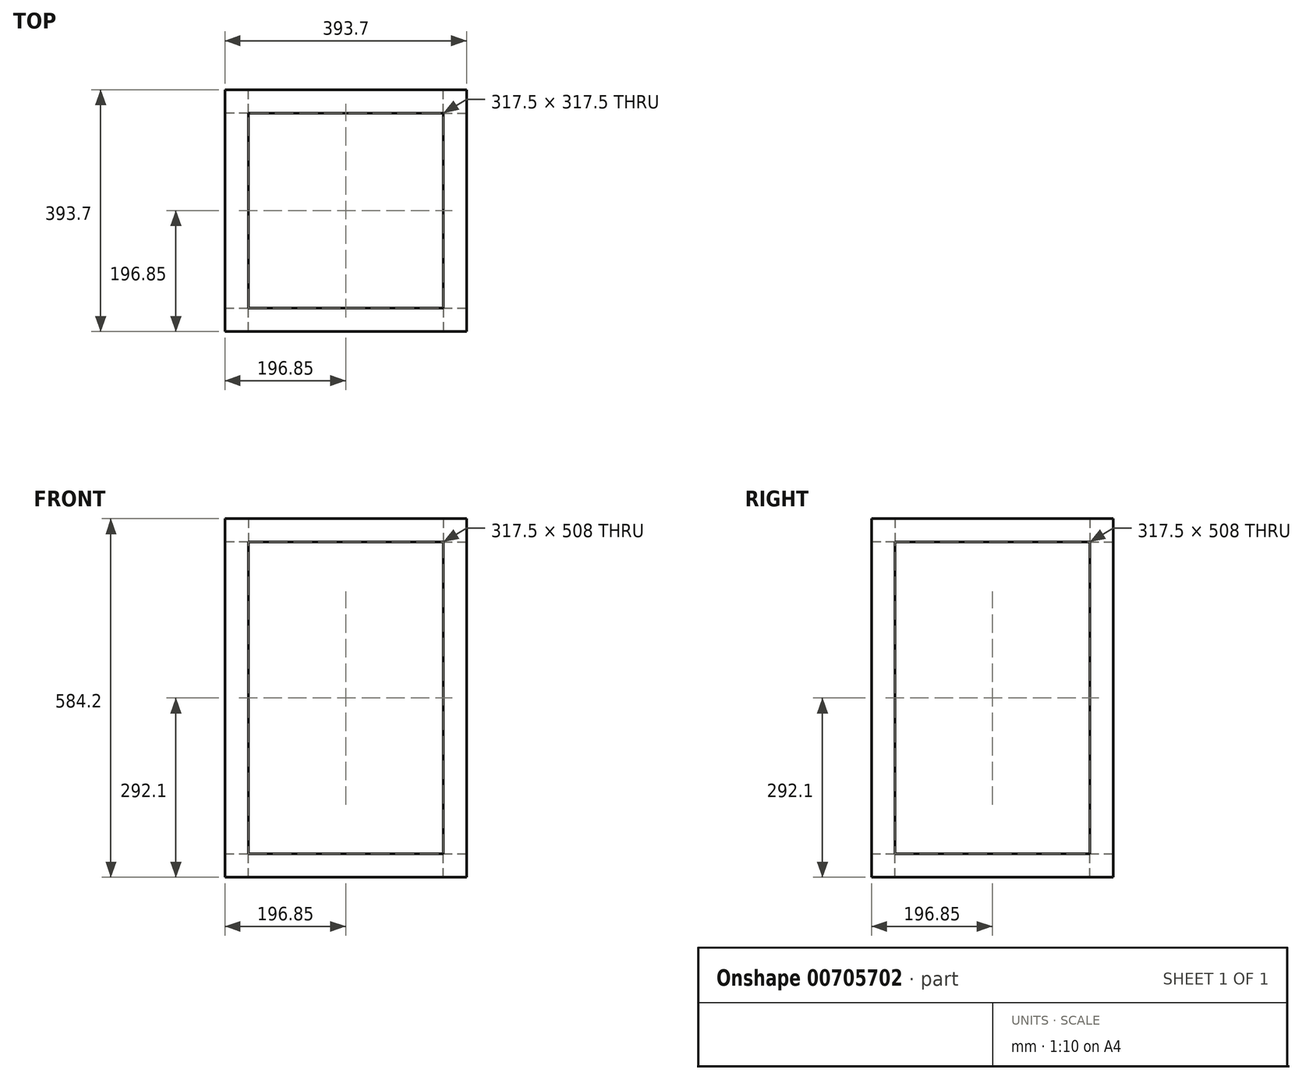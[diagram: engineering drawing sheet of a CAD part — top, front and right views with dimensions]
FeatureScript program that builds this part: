
annotation { "Feature Type Name" : "Feature", "Feature Type Description" : "" }
export const myFeature = defineFeature(function(context is Context, id is Id, definition is map)
    precondition{}
    {
        {
            var Q0;
            Q0=qCreatedBy(makeId("Top.planeOp"),FACE);
            var sketch = newSketch(context, id + "F0", { "sketchPlane" : qUnion([Q0])});
            skLineSegment(sketch, "E0.bottom", {"start": v(196.85, 196.85) * mm, "end": v(-196.85, 196.85) * mm});
            skLineSegment(sketch, "E0.top", {"start": v(196.85, -196.85) * mm, "end": v(-196.85, -196.85) * mm});
            skLineSegment(sketch, "E0.left", {"start": v(196.85, 196.85) * mm, "end": v(196.85, -196.85) * mm});
            skLineSegment(sketch, "E0.right", {"start": v(-196.85, 196.85) * mm, "end": v(-196.85, -196.85) * mm});
            skPoint(sketch, "E0.middle", {"position": v(0, 0) * mm});
            skLineSegment(sketch, "E1.0", {"start": v(-158.75, 158.75) * mm, "end": v(-158.75, -158.75) * mm});
            skLineSegment(sketch, "E1.1", {"start": v(158.75, 158.75) * mm, "end": v(-158.75, 158.75) * mm});
            skLineSegment(sketch, "E1.2", {"start": v(158.75, 158.75) * mm, "end": v(158.75, -158.75) * mm});
            skLineSegment(sketch, "E1.3", {"start": v(158.75, -158.75) * mm, "end": v(-158.75, -158.75) * mm});
            skSolve(sketch);
        }
        {
            var Q0;
            Q0 = qSketchRegion(id + "F0", true);
            extrude(context, id + "F1", {"entities" : qUnion([Q0]), "depth" : 38.1 * mm, "offsetDistance" : 25.4 * mm});
        }
        {
            var Q0;
            Q0=makeQuery(id+"F1.opExtrude","CAP_FACE",FACE,{"disambiguationData":[OSD([sQuery(id+"F0.wireOp",EDGE,"E0.bottom"),sQuery(id+"F0.wireOp",EDGE,"E0.top"),sQuery(id+"F0.wireOp",EDGE,"E0.left"),sQuery(id+"F0.wireOp",EDGE,"E0.right"),sQuery(id+"F0.wireOp",EDGE,"E1.0"),sQuery(id+"F0.wireOp",EDGE,"E1.1"),sQuery(id+"F0.wireOp",EDGE,"E1.2"),sQuery(id+"F0.wireOp",EDGE,"E1.3")])],"isStart":true});
            var sketch = newSketch(context, id + "F2", { "sketchPlane" : qUnion([Q0])});
            skLineSegment(sketch, "E2.bottom", {"start": v(-196.85, 196.85) * mm, "end": v(-158.75, 196.85) * mm});
            skLineSegment(sketch, "E2.top", {"start": v(-196.85, 158.75) * mm, "end": v(-158.75, 158.75) * mm});
            skLineSegment(sketch, "E2.left", {"start": v(-196.85, 196.85) * mm, "end": v(-196.85, 158.75) * mm});
            skLineSegment(sketch, "E2.right", {"start": v(-158.75, 196.85) * mm, "end": v(-158.75, 158.75) * mm});
            skLineSegment(sketch, "E3.bottom", {"start": v(-158.75, -158.75) * mm, "end": v(-196.85, -158.75) * mm});
            skLineSegment(sketch, "E3.top", {"start": v(-158.75, -196.85) * mm, "end": v(-196.85, -196.85) * mm});
            skLineSegment(sketch, "E3.left", {"start": v(-158.75, -158.75) * mm, "end": v(-158.75, -196.85) * mm});
            skLineSegment(sketch, "E3.right", {"start": v(-196.85, -158.75) * mm, "end": v(-196.85, -196.85) * mm});
            skLineSegment(sketch, "E4.bottom", {"start": v(158.75, 158.75) * mm, "end": v(196.85, 158.75) * mm});
            skLineSegment(sketch, "E4.top", {"start": v(158.75, 196.85) * mm, "end": v(196.85, 196.85) * mm});
            skLineSegment(sketch, "E4.left", {"start": v(158.75, 158.75) * mm, "end": v(158.75, 196.85) * mm});
            skLineSegment(sketch, "E4.right", {"start": v(196.85, 158.75) * mm, "end": v(196.85, 196.85) * mm});
            skLineSegment(sketch, "E5.bottom", {"start": v(158.75, -158.75) * mm, "end": v(196.85, -158.75) * mm});
            skLineSegment(sketch, "E5.top", {"start": v(158.75, -196.85) * mm, "end": v(196.85, -196.85) * mm});
            skLineSegment(sketch, "E5.left", {"start": v(158.75, -158.75) * mm, "end": v(158.75, -196.85) * mm});
            skLineSegment(sketch, "E5.right", {"start": v(196.85, -158.75) * mm, "end": v(196.85, -196.85) * mm});
            skSolve(sketch);
        }
        {
            var Q0;
            Q0 = qSketchRegion(id + "F2", true);
            extrude(context, id + "F3", {"entities" : qUnion([Q0]), "operationType" : NewBodyOperationType.ADD, "depth" : 508 * mm, "offsetDistance" : 25.4 * mm});
        }
        {
            var Q0;
            Q0=makeQuery(id+"F3.opExtrude","CAP_FACE",FACE,{"disambiguationData":[OSD([sQuery(id+"F2.wireOp",EDGE,"E5.bottom"),sQuery(id+"F2.wireOp",EDGE,"E5.top"),sQuery(id+"F2.wireOp",EDGE,"E5.left"),sQuery(id+"F2.wireOp",EDGE,"E5.right")])],"isStart":false});
            var sketch = newSketch(context, id + "F4", { "sketchPlane" : qUnion([Q0])});
            skLineSegment(sketch, "E6.0", {"start": v(196.85, -196.85) * mm, "end": v(158.75, -196.85) * mm});
            skLineSegment(sketch, "E6.1", {"start": v(158.75, -196.85) * mm, "end": v(-158.75, -196.85) * mm});
            skLineSegment(sketch, "E6.2", {"start": v(-158.75, -196.85) * mm, "end": v(-196.85, -196.85) * mm});
            skLineSegment(sketch, "E6.3", {"start": v(-196.85, -196.85) * mm, "end": v(-196.85, -158.75) * mm});
            skLineSegment(sketch, "E6.4", {"start": v(-196.85, -158.75) * mm, "end": v(-196.85, 158.75) * mm});
            skLineSegment(sketch, "E6.5", {"start": v(-196.85, 158.75) * mm, "end": v(-196.85, 196.85) * mm});
            skLineSegment(sketch, "E6.6", {"start": v(-158.75, 196.85) * mm, "end": v(-196.85, 196.85) * mm});
            skLineSegment(sketch, "E6.7", {"start": v(158.75, 196.85) * mm, "end": v(-158.75, 196.85) * mm});
            skLineSegment(sketch, "E6.8", {"start": v(196.85, 196.85) * mm, "end": v(158.75, 196.85) * mm});
            skLineSegment(sketch, "E6.9", {"start": v(196.85, 158.75) * mm, "end": v(196.85, 196.85) * mm});
            skLineSegment(sketch, "E6.10", {"start": v(196.85, -158.75) * mm, "end": v(196.85, 158.75) * mm});
            skLineSegment(sketch, "E6.11", {"start": v(196.85, -196.85) * mm, "end": v(196.85, -158.75) * mm});
            skLineSegment(sketch, "E7.1", {"start": v(158.75, -158.75) * mm, "end": v(-158.75, -158.75) * mm});
            skLineSegment(sketch, "E7.2", {"start": v(158.75, -158.75) * mm, "end": v(158.75, 158.75) * mm});
            skLineSegment(sketch, "E7.3", {"start": v(158.75, 158.75) * mm, "end": v(-158.75, 158.75) * mm});
            skLineSegment(sketch, "E7.4", {"start": v(-158.75, -158.75) * mm, "end": v(-158.75, 158.75) * mm});
            skSolve(sketch);
        }
        {
            var Q0;
            Q0 = qSketchRegion(id + "F4", true);
            extrude(context, id + "F5", {"entities" : qUnion([Q0]), "operationType" : NewBodyOperationType.ADD, "depth" : 38.1 * mm, "offsetDistance" : 25.4 * mm});
        }
    });
